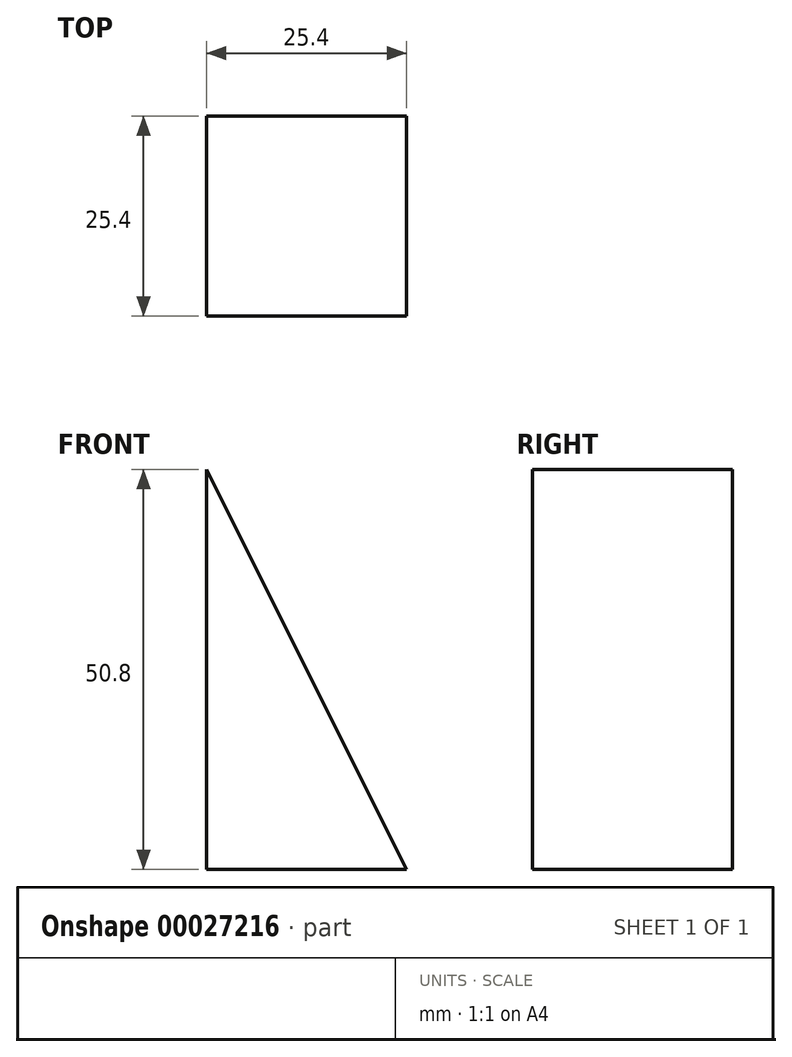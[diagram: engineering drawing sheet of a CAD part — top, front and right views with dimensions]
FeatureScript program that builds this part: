
annotation { "Feature Type Name" : "Feature", "Feature Type Description" : "" }
export const myFeature = defineFeature(function(context is Context, id is Id, definition is map)
    precondition{}
    {
        {
            var Q0;
            Q0=qCreatedBy(makeId("Front.planeOp"),FACE);
            var sketch = newSketch(context, id + "F0", { "sketchPlane" : qUnion([Q0])});
            skLineSegment(sketch, "E0", {"start": v(0, 0) * mm, "end": v(0, 50.8) * mm});
            skLineSegment(sketch, "E1", {"start": v(0, 50.8) * mm, "end": v(25.4, 0) * mm});
            skLineSegment(sketch, "E2", {"start": v(25.4, 0) * mm, "end": v(0, 0) * mm});
            skSolve(sketch);
        }
        {
            var Q0;
            Q0=makeQuery(id+"F0.imprint","IMPRINT",FACE,{"disambiguationData":[TD([[makeQuery(id+"F0.imprint","IMPRINT",EDGE,{"derivedFrom":sQuery(id+"F0.wireOp",EDGE,"E0")}),-1.0]])]});
            extrude(context, id + "F1", {"entities" : qUnion([Q0]), "depth" : 25.4 * mm});
        }
    });
